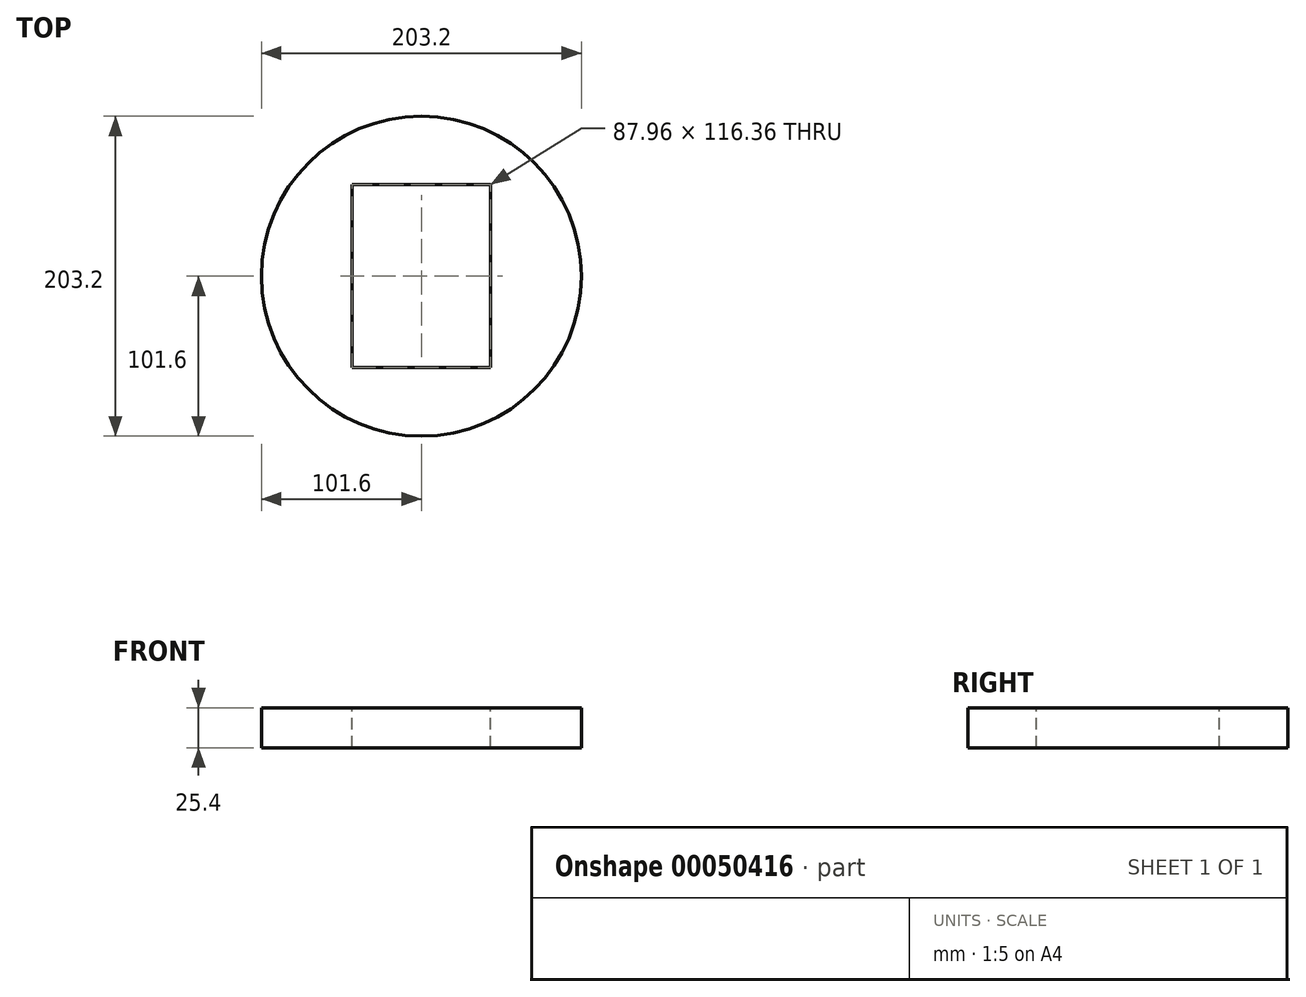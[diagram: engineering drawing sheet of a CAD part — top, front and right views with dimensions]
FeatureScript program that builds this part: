
annotation { "Feature Type Name" : "Feature", "Feature Type Description" : "" }
export const myFeature = defineFeature(function(context is Context, id is Id, definition is map)
    precondition{}
    {
        {
            var Q0;
            Q0=qCreatedBy(makeId("Top.planeOp"),FACE);
            var sketch = newSketch(context, id + "F0", { "sketchPlane" : qUnion([Q0])});
            skCircle(sketch, "E0", {"center": v(0, 0) * mm, "radius": 101.6 * mm});
            skSolve(sketch);
        }
        {
            var Q0;
            Q0=makeQuery(id+"F0.imprint","IMPRINT",FACE,{"disambiguationData":[TD([[makeQuery(id+"F0.imprint","IMPRINT",EDGE,{"derivedFrom":sQuery(id+"F0.wireOp",EDGE,"E0")}),1.0]])]});
            extrude(context, id + "F1", {"entities" : qUnion([Q0]), "depth" : 25.4 * mm});
        }
        {
            var Q0;
            Q0=makeQuery(id+"F1.opExtrude","CAP_FACE",FACE,{"disambiguationData":[OSD([sQuery(id+"F0.wireOp",EDGE,"E0")])],"isStart":false});
            var sketch = newSketch(context, id + "F2", { "sketchPlane" : qUnion([Q0])});
            skLineSegment(sketch, "E1.rect.bottom", {"start": v(43.98, -58.18) * mm, "end": v(-43.98, -58.18) * mm});
            skLineSegment(sketch, "E1.rect.top", {"start": v(43.98, 58.18) * mm, "end": v(-43.98, 58.18) * mm});
            skLineSegment(sketch, "E1.rect.left", {"start": v(43.98, -58.18) * mm, "end": v(43.98, 58.18) * mm});
            skLineSegment(sketch, "E1.rect.right", {"start": v(-43.98, -58.18) * mm, "end": v(-43.98, 58.18) * mm});
            skPoint(sketch, "E1.rect.middle", {"position": v(0, 0) * mm});
            skSolve(sketch);
        }
        {
            var Q0;
            Q0=makeQuery(id+"F2.imprint","IMPRINT",FACE,{"disambiguationData":[TD([[makeQuery(id+"F2.imprint","IMPRINT",EDGE,{"derivedFrom":sQuery(id+"F2.wireOp",EDGE,"E1.rect.bottom")}),-1.0]])]});
            extrude(context, id + "F3", {"entities" : qUnion([Q0]), "operationType" : NewBodyOperationType.REMOVE, "oppositeDirection" : true, "depth" : 25.4 * mm});
        }
    });
